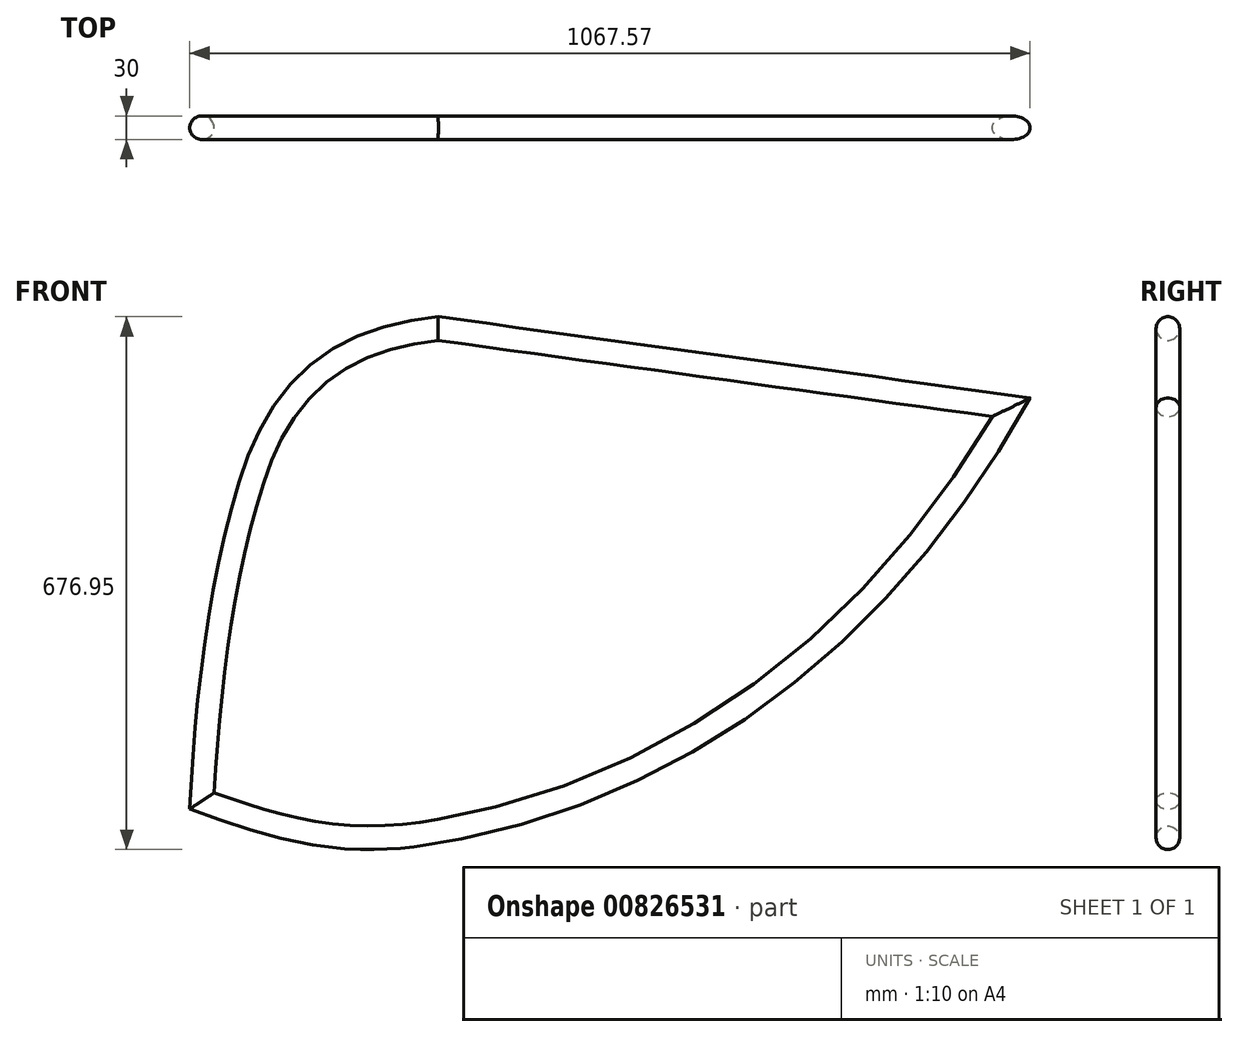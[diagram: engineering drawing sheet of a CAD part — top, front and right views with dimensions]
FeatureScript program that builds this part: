
annotation { "Feature Type Name" : "Feature", "Feature Type Description" : "" }
export const myFeature = defineFeature(function(context is Context, id is Id, definition is map)
    precondition{}
    {
        {
            var Q0;
            Q0=qCreatedBy(makeId("Front.planeOp"),FACE);
            var sketch = newSketch(context, id + "F0", { "sketchPlane" : qUnion([Q0])});
            skPoint(sketch, "E0", {"position": v(0, 0) * mm});
            skPoint(sketch, "E1", {"position": v(300, 600) * mm});
            skLineSegment(sketch, "E2", {"start": v(1028.01, 500) * mm, "end": v(300, 600) * mm});
            skFitSpline(sketch, "E3", {"points": [v(300, 600) * mm, v(50.12, 361.16) * mm, v(0, 0) * mm], "startDerivative": vector(-1053.16, -107.12) * mm, "endDerivative": vector(-36.95, -694.76) * mm});
            skFitSpline(sketch, "E4", {"points": [v(1028.01, 500) * mm, v(310.87, -36.9) * mm, v(0, 0) * mm], "startDerivative": vector(-1041.92, -1821.9) * mm, "endDerivative": vector(-1036.32, 382.22) * mm});
            skSolve(sketch);
        }
        {
            var Q0;
            Q0=sQuery(id+"F0.wireOp",VERTEX,"E2.start");
            var Q1;
            Q1=sQuery(id+"F0.wireOp",EDGE,"E2");
            cPlane(context, id + "F1", {"entities" : qUnion([Q0, Q1]), "cplaneType" : CPlaneType.LINE_POINT, "offset" : 25 * mm, "width" : 150 * mm, "height" : 150 * mm});
        }
        {
            var Q0;
            Q0=sQuery(id+"F0.wireOp",VERTEX,"E1");
            var Q1;
            Q1=sQuery(id+"F0.wireOp",EDGE,"E2");
            cPlane(context, id + "F2", {"entities" : qUnion([Q0, Q1]), "cplaneType" : CPlaneType.LINE_POINT, "offset" : 25 * mm, "width" : 150 * mm, "height" : 150 * mm});
        }
        {
            var Q0;
            Q0=qCreatedBy(makeId("Top.planeOp"),FACE);
            var sketch = newSketch(context, id + "F3", { "sketchPlane" : qUnion([Q0])});
            skCircle(sketch, "E5", {"center": v(0, 0) * mm, "radius": 15 * mm});
            skSolve(sketch);
        }
        {
            var Q0;
            Q0=makeQuery(id+"F3.imprint","IMPRINT",FACE,{"disambiguationData":[TD([[makeQuery(id+"F3.imprint","IMPRINT",EDGE,{"derivedFrom":sQuery(id+"F3.wireOp",EDGE,"E5")}),1.0]])]});
            var Q1;
            Q1=sQuery(id+"F0.wireOp",EDGE,"E3");
            var Q2;
            Q2=sQuery(id+"F0.wireOp",EDGE,"E2");
            var Q3;
            Q3=sQuery(id+"F0.wireOp",EDGE,"E4");
            sweep(context, id + "F4", {"profiles" : qUnion([Q0]), "path" : qUnion([Q1, Q2, Q3])});
        }
    });
